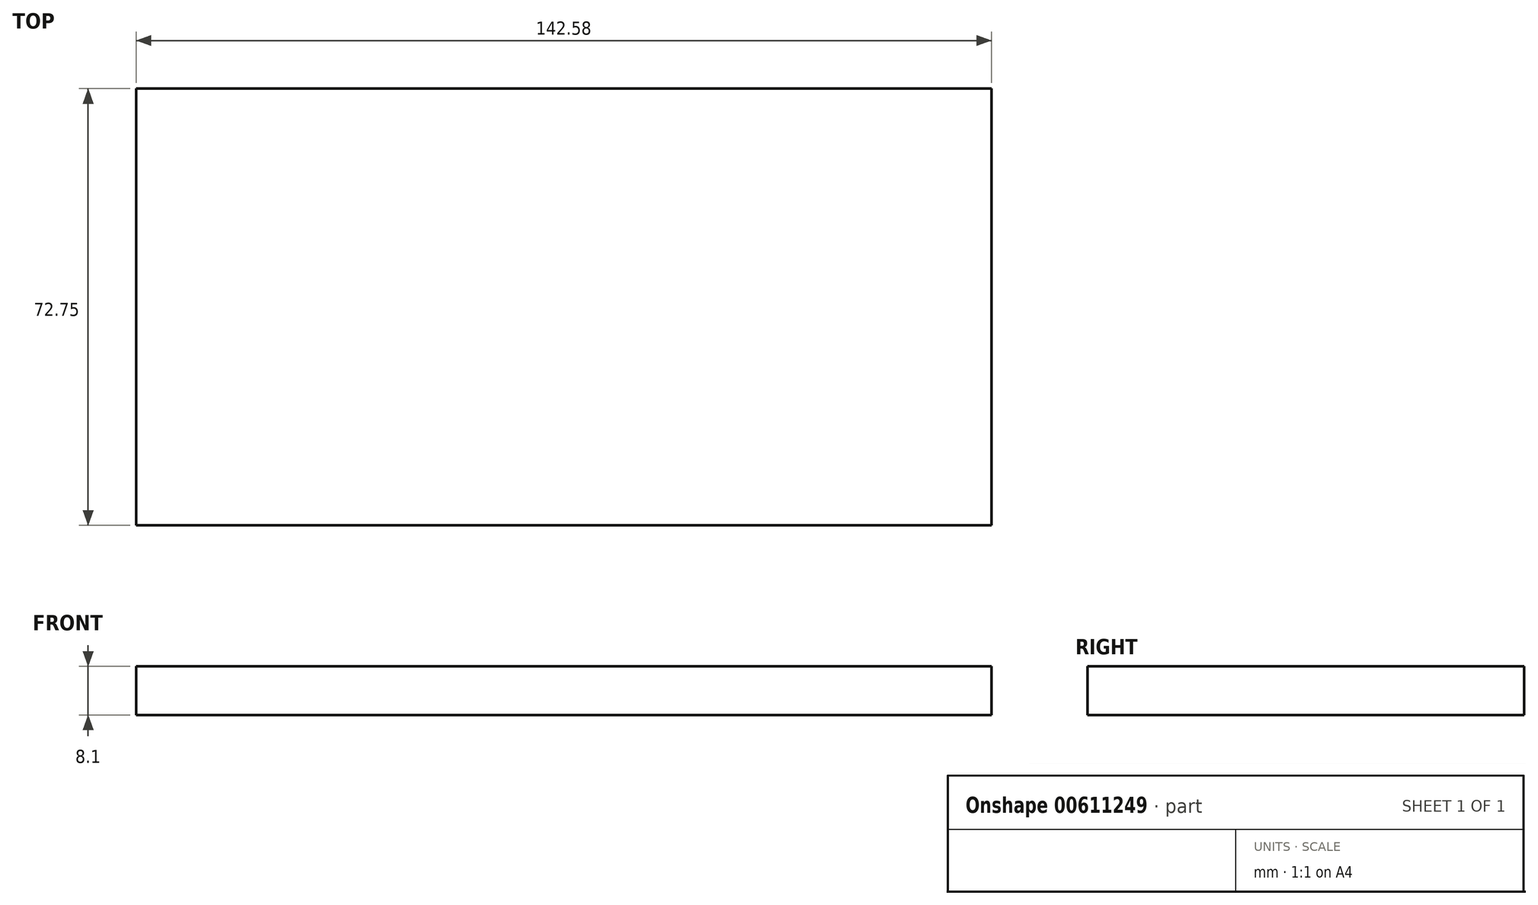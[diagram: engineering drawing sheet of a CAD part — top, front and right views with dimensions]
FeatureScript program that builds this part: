
annotation { "Feature Type Name" : "Feature", "Feature Type Description" : "" }
export const myFeature = defineFeature(function(context is Context, id is Id, definition is map)
    precondition{}
    {
        {
            var Q0;
            Q0=qCreatedBy(makeId("Top.planeOp"),FACE);
            var sketch = newSketch(context, id + "F0", { "sketchPlane" : qUnion([Q0])});
            skLineSegment(sketch, "E0.bottom", {"start": v(-69.65, 24.36) * mm, "end": v(72.93, 24.36) * mm});
            skLineSegment(sketch, "E0.top", {"start": v(-69.65, -48.39) * mm, "end": v(72.93, -48.39) * mm});
            skLineSegment(sketch, "E0.left", {"start": v(-69.65, 24.36) * mm, "end": v(-69.65, -48.39) * mm});
            skLineSegment(sketch, "E0.right", {"start": v(72.93, 24.36) * mm, "end": v(72.93, -48.39) * mm});
            skSolve(sketch);
        }
        {
            var Q0;
            Q0=makeQuery(id+"F0.imprint","IMPRINT",FACE,{"disambiguationData":[TD([[makeQuery(id+"F0.imprint","IMPRINT",EDGE,{"derivedFrom":sQuery(id+"F0.wireOp",EDGE,"E0.bottom")}),-1.0]])]});
            extrude(context, id + "F1", {"entities" : qUnion([Q0]), "depth" : 8.1 * mm, "offsetDistance" : 25 * mm});
        }
    });
